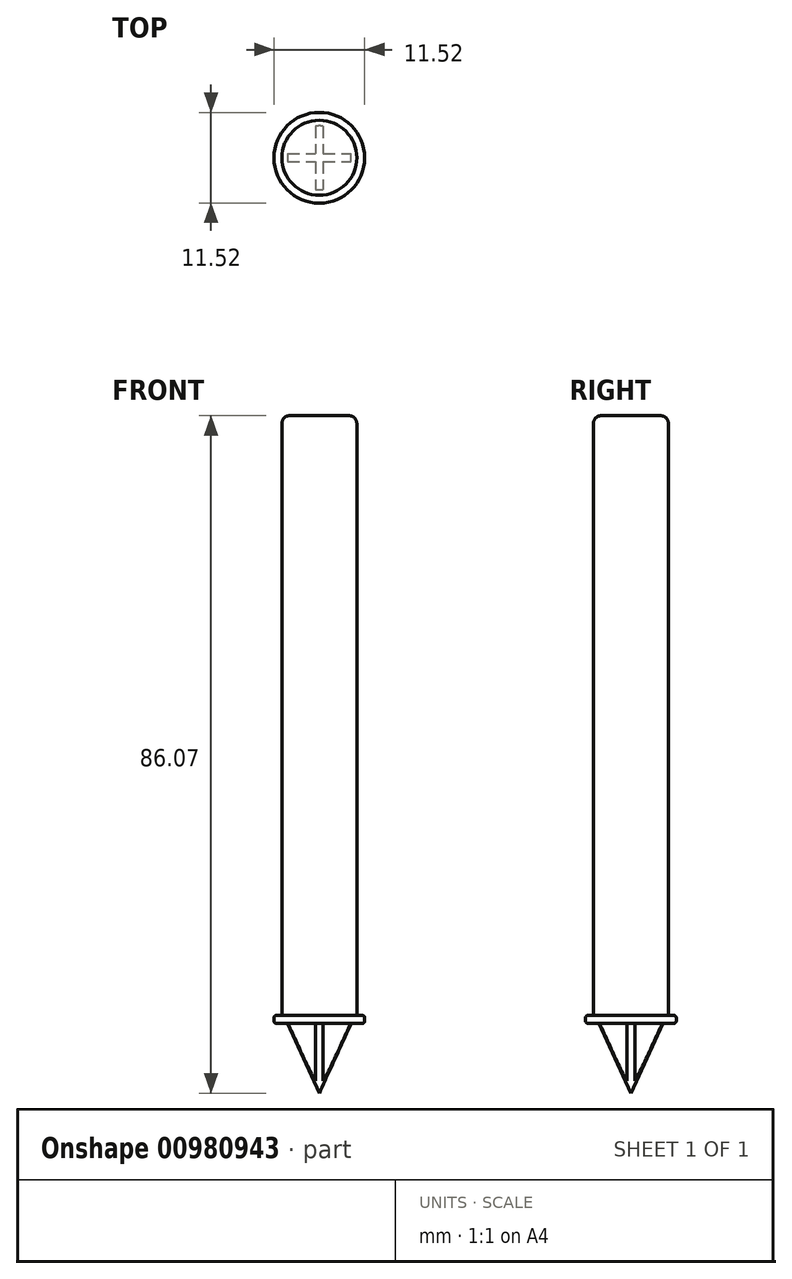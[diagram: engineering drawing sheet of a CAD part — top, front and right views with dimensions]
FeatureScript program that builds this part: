
annotation { "Feature Type Name" : "Feature", "Feature Type Description" : "" }
export const myFeature = defineFeature(function(context is Context, id is Id, definition is map)
    precondition{}
    {
        {
            var Q0;
            Q0=qCreatedBy(makeId("Top.planeOp"),FACE);
            var sketch = newSketch(context, id + "F0", { "sketchPlane" : qUnion([Q0])});
            skCircle(sketch, "E0", {"center": v(0, 0) * mm, "radius": 4.76 * mm});
            skSolve(sketch);
        }
        {
            var Q0;
            Q0=makeQuery(id+"F0.imprint","IMPRINT",FACE,{"disambiguationData":[TD([[makeQuery(id+"F0.imprint","IMPRINT",EDGE,{"derivedFrom":sQuery(id+"F0.wireOp",EDGE,"E0")}),1.0]])]});
            extrude(context, id + "F1", {"entities" : qUnion([Q0]), "depth" : 76.2 * mm, "offsetDistance" : 25 * mm});
        }
        {
            var Q0;
            Q0=qCreatedBy(makeId("Top.planeOp"),FACE);
            var sketch = newSketch(context, id + "F2", { "sketchPlane" : qUnion([Q0])});
            skCircle(sketch, "E1", {"center": v(0, 0) * mm, "radius": 5.76 * mm});
            skSolve(sketch);
        }
        {
            var Q0;
            Q0=makeQuery(id+"F2.imprint","IMPRINT",FACE,{"disambiguationData":[TD([[makeQuery(id+"F2.imprint","IMPRINT",EDGE,{"derivedFrom":sQuery(id+"F2.wireOp",EDGE,"E1")}),1.0]])]});
            extrude(context, id + "F3", {"entities" : qUnion([Q0]), "operationType" : NewBodyOperationType.ADD, "oppositeDirection" : true, "depth" : 1 * mm, "offsetDistance" : 25 * mm});
        }
        {
            var Q0;
            Q0=qCreatedBy(makeId("Right.planeOp"),FACE);
            var sketch = newSketch(context, id + "F4", { "sketchPlane" : qUnion([Q0])});
            skLineSegment(sketch, "E2", {"start": v(0, -0.96) * mm, "end": v(0, -9.87) * mm});
            skLineSegment(sketch, "E3", {"start": v(0, -9.87) * mm, "end": v(-4.07, -0.96) * mm});
            skLineSegment(sketch, "E4", {"start": v(-4.07, -0.96) * mm, "end": v(0, -0.96) * mm});
            skSolve(sketch);
        }
        {
            var Q0;
            Q0=makeQuery(id+"F4.imprint","IMPRINT",FACE,{"disambiguationData":[TD([[makeQuery(id+"F4.imprint","IMPRINT",EDGE,{"derivedFrom":sQuery(id+"F4.wireOp",EDGE,"E2")}),-1.0]])]});
            var Q1;
            Q1=sQuery(id+"F4.wireOp",EDGE,"E2");
            revolve(context, id + "F5", {"operationType" : NewBodyOperationType.ADD, "surfaceOperationType" : NewSurfaceOperationType.NEW, "entities" : qUnion([Q0]), "axis" : qUnion([Q1]), "revolveType" : RevolveType.FULL});
        }
        {
            var Q0;
            Q0=makeQuery(id+"F3.opExtrude","CAP_FACE",FACE,{"disambiguationData":[OSD([sQuery(id+"F2.wireOp",EDGE,"E1")])],"isStart":false});
            var sketch = newSketch(context, id + "F6", { "sketchPlane" : qUnion([Q0])});
            skLineSegment(sketch, "E5.0", {"start": v(0.5, -4.05) * mm, "end": v(0.5, -0.5) * mm});
            skLineSegment(sketch, "E6.0", {"start": v(-0.5, -4.05) * mm, "end": v(-0.5, -0.5) * mm});
            skLineSegment(sketch, "E7.0", {"start": v(-4.05, -0.5) * mm, "end": v(-0.5, -0.5) * mm});
            skLineSegment(sketch, "E8.0", {"start": v(-4.05, 0.5) * mm, "end": v(-0.5, 0.5) * mm});
            skLineSegment(sketch, "E9.trimOffspring", {"start": v(0.5, -0.5) * mm, "end": v(4.05, -0.5) * mm});
            skLineSegment(sketch, "E10.trimOffspring", {"start": v(0.5, 0.5) * mm, "end": v(0.5, 4.05) * mm});
            skLineSegment(sketch, "E11.trimOffspring", {"start": v(0.5, 0.5) * mm, "end": v(4.05, 0.5) * mm});
            skPoint(sketch, "E12.orphan", {"position": v(0, -4.05) * mm});
            skLineSegment(sketch, "E13.trimOffspring", {"start": v(-0.5, 0.5) * mm, "end": v(-0.5, 4.05) * mm});
            skPoint(sketch, "E14.start.orphan", {"position": v(-4.05, 0) * mm});
            skArc(sketch, "E15", {"start": v(-0.5, 4.05) * mm, "mid": v(-2.89, 2.89) * mm, "end": v(-4.05, 0.5) * mm});
            skArc(sketch, "E16", {"start": v(-4.05, -0.5) * mm, "mid": v(-2.89, -2.89) * mm, "end": v(-0.5, -4.05) * mm});
            skArc(sketch, "E17", {"start": v(0.5, -4.05) * mm, "mid": v(2.89, -2.89) * mm, "end": v(4.05, -0.5) * mm});
            skArc(sketch, "E18", {"start": v(0.5, 4.05) * mm, "mid": v(2.89, 2.89) * mm, "end": v(4.05, 0.5) * mm});
            skSolve(sketch);
        }
        {
            var Q0;
            Q0 = qSketchRegion(id + "F6", true);
            extrude(context, id + "F7", {"entities" : qUnion([Q0]), "operationType" : NewBodyOperationType.REMOVE, "depth" : 25 * mm, "offsetDistance" : 25 * mm});
        }
        {
            var Q0;
            Q0=makeQuery(id+"F1.opExtrude","CAP_EDGE",EDGE,{"disambiguationData":[OSD([sQuery(id+"F0.wireOp",EDGE,"E0")])],"isStart":false});
            fillet(context, id + "F8", {"entities" : qUnion([Q0]), "radius" : 1 * mm, "tangentPropagation" : true, "allowEdgeOverflow" : false});
        }
        {
            var Q0;
            Q0=makeQuery(id+"F3.opExtrude","CAP_EDGE",EDGE,{"disambiguationData":[OSD([sQuery(id+"F2.wireOp",EDGE,"E1")])],"isStart":true});
            var Q1;
            Q1=makeQuery(id+"F3.opExtrude","CAP_EDGE",EDGE,{"disambiguationData":[OSD([sQuery(id+"F2.wireOp",EDGE,"E1")])],"isStart":false});
            fillet(context, id + "F9", {"entities" : qUnion([Q0, Q1]), "radius" : 0.3 * mm, "tangentPropagation" : true, "allowEdgeOverflow" : false});
        }
    });
